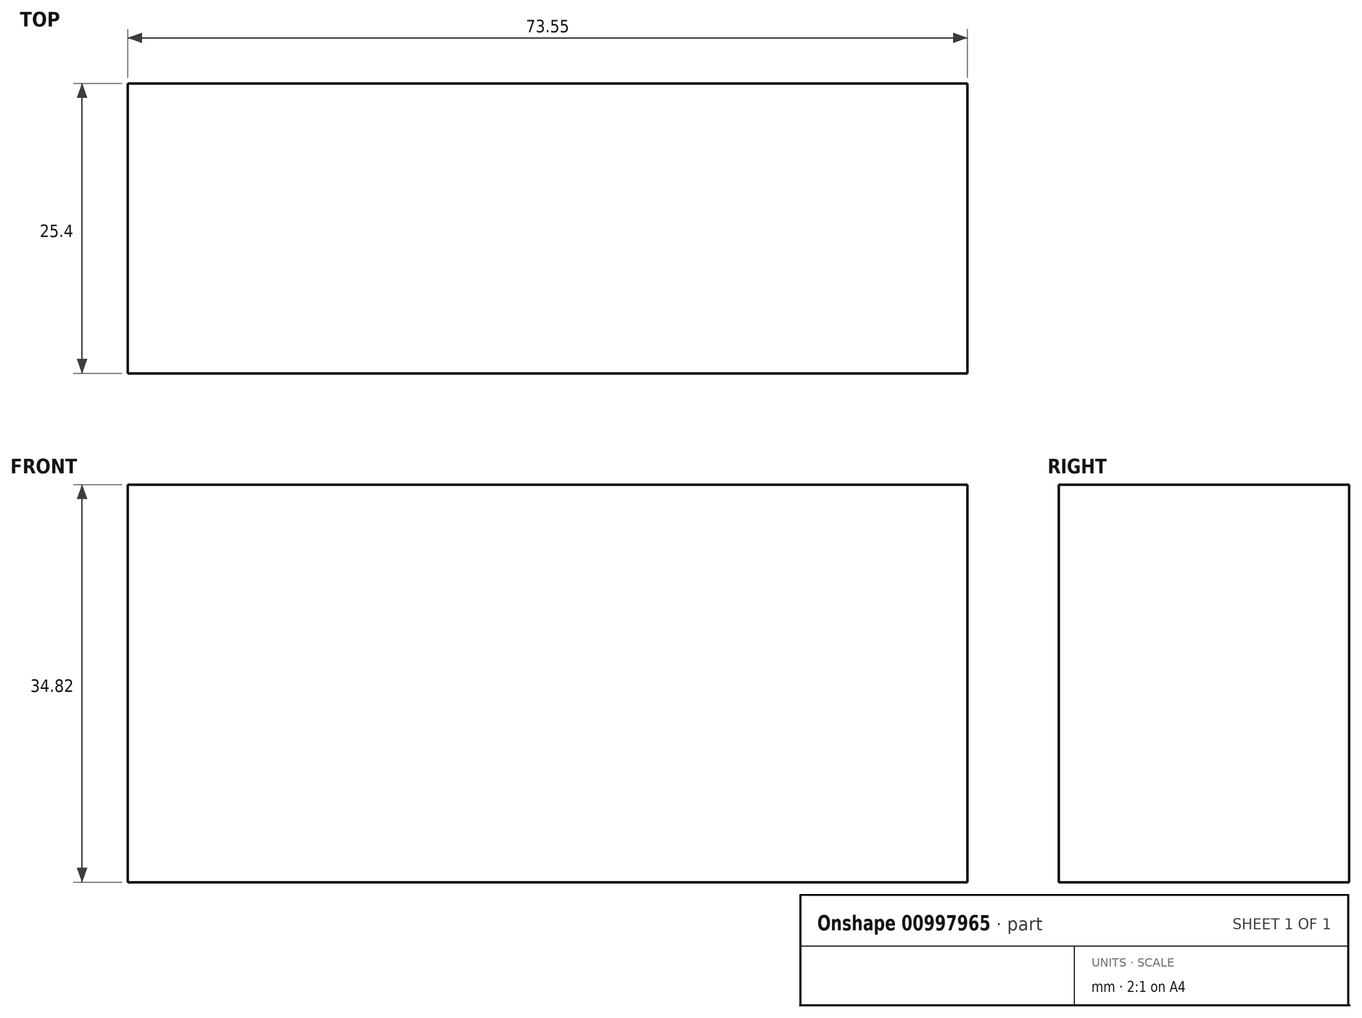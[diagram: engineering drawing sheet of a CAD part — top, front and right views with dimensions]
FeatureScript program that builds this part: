
annotation { "Feature Type Name" : "Feature", "Feature Type Description" : "" }
export const myFeature = defineFeature(function(context is Context, id is Id, definition is map)
    precondition{}
    {
        {
            var Q0;
            Q0=qCreatedBy(makeId("Front.planeOp"),FACE);
            var sketch = newSketch(context, id + "F0", { "sketchPlane" : qUnion([Q0])});
            skLineSegment(sketch, "E0.bottom", {"start": v(-28.75, 34.82) * mm, "end": v(44.8, 34.82) * mm});
            skLineSegment(sketch, "E0.top", {"start": v(-28.75, 0) * mm, "end": v(44.8, 0) * mm});
            skLineSegment(sketch, "E0.left", {"start": v(-28.75, 34.82) * mm, "end": v(-28.75, 0) * mm});
            skLineSegment(sketch, "E0.right", {"start": v(44.8, 34.82) * mm, "end": v(44.8, 0) * mm});
            skSolve(sketch);
        }
        {
            var Q0;
            Q0 = qSketchRegion(id + "F0", true);
            extrude(context, id + "F1", {"entities" : qUnion([Q0]), "depth" : 25.4 * mm, "offsetDistance" : 25.4 * mm});
        }
    });
